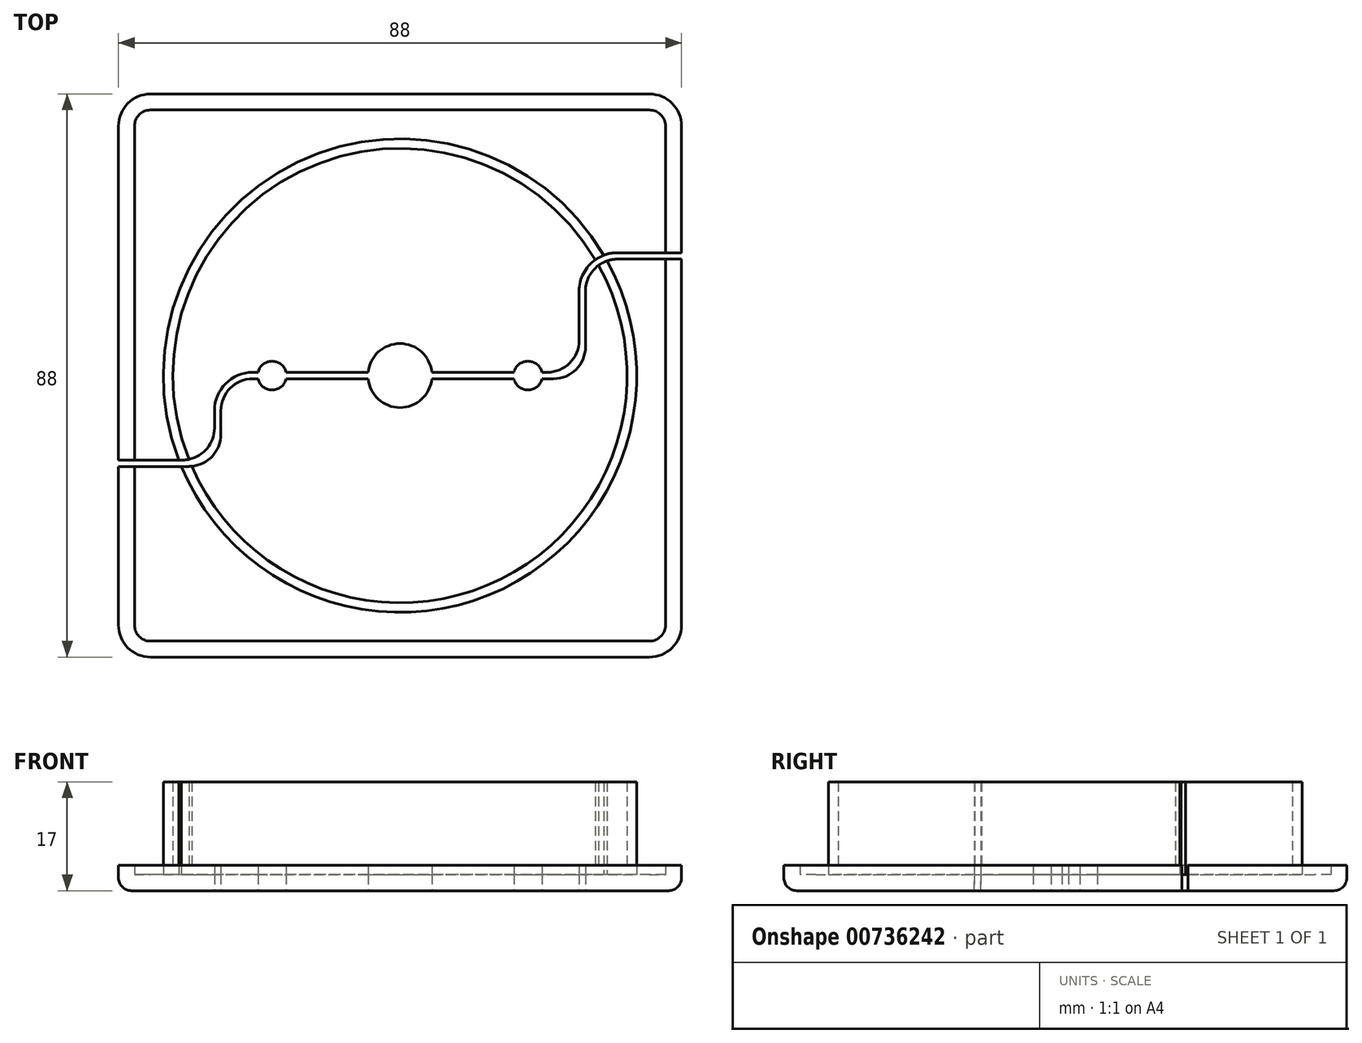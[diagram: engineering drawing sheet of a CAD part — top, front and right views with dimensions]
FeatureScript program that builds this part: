
annotation { "Feature Type Name" : "Feature", "Feature Type Description" : "" }
export const myFeature = defineFeature(function(context is Context, id is Id, definition is map)
    precondition{}
    {
        {
            var Q0;
            Q0=qCreatedBy(makeId("Top.planeOp"),FACE);
            var sketch = newSketch(context, id + "F0", { "sketchPlane" : qUnion([Q0])});
            skPoint(sketch, "E0.middle", {"position": v(0, 0) * mm});
            skLineSegment(sketch, "E1.bottom", {"start": v(39, -44) * mm, "end": v(-39, -44) * mm});
            skLineSegment(sketch, "E1.top", {"start": v(39, 44) * mm, "end": v(-39, 44) * mm});
            skLineSegment(sketch, "E1.left", {"start": v(44, -39) * mm, "end": v(44, 39) * mm});
            skLineSegment(sketch, "E1.right", {"start": v(-44, -39) * mm, "end": v(-44, 39) * mm});
            skPoint(sketch, "E2.visualSharp", {"position": v(-44, 44) * mm});
            skArc(sketch, "E2.filletArc", {"start": v(-39, 44) * mm, "mid": v(-42.54, 42.54) * mm, "end": v(-44, 39) * mm});
            skPoint(sketch, "E3.visualSharp", {"position": v(44, 44) * mm});
            skArc(sketch, "E3.filletArc", {"start": v(44, 39) * mm, "mid": v(42.54, 42.54) * mm, "end": v(39, 44) * mm});
            skPoint(sketch, "E4.visualSharp", {"position": v(44, -44) * mm});
            skArc(sketch, "E4.filletArc", {"start": v(39, -44) * mm, "mid": v(42.54, -42.54) * mm, "end": v(44, -39) * mm});
            skPoint(sketch, "E5.visualSharp", {"position": v(-44, -44) * mm});
            skArc(sketch, "E5.filletArc", {"start": v(-44, -39) * mm, "mid": v(-42.54, -42.54) * mm, "end": v(-39, -44) * mm});
            skSolve(sketch);
        }
        {
            var Q0;
            Q0=makeQuery(id+"F0.imprint","IMPRINT",FACE,{"disambiguationData":[TD([[makeQuery(id+"F0.imprint","IMPRINT",EDGE,{"derivedFrom":sQuery(id+"F0.wireOp",EDGE,"E1.bottom")}),-1.0]])]});
            extrude(context, id + "F1", {"entities" : qUnion([Q0]), "depth" : 4 * mm, "offsetDistance" : 25 * mm});
        }
        {
            var Q0;
            Q0=makeQuery(id+"F1.opExtrude","CAP_FACE",FACE,{"disambiguationData":[OSD([sQuery(id+"F0.wireOp",EDGE,"E1.bottom"),sQuery(id+"F0.wireOp",EDGE,"E1.top"),sQuery(id+"F0.wireOp",EDGE,"E1.left"),sQuery(id+"F0.wireOp",EDGE,"E1.right"),sQuery(id+"F0.wireOp",EDGE,"E2.filletArc"),sQuery(id+"F0.wireOp",EDGE,"E3.filletArc"),sQuery(id+"F0.wireOp",EDGE,"E4.filletArc"),sQuery(id+"F0.wireOp",EDGE,"E5.filletArc")])],"isStart":false});
            shell(context, id + "F2", {"entities" : qUnion([Q0]), "thickness" : 2.5 * mm});
        }
        {
            var Q0;
            Q0=makeQuery(id+"F2.opShell","OFFSET_FACE",FACE,{"disambiguationData":[OSD([sQuery(id+"F0.wireOp",EDGE,"E1.bottom"),sQuery(id+"F0.wireOp",EDGE,"E1.top"),sQuery(id+"F0.wireOp",EDGE,"E1.left"),sQuery(id+"F0.wireOp",EDGE,"E1.right"),sQuery(id+"F0.wireOp",EDGE,"E2.filletArc"),sQuery(id+"F0.wireOp",EDGE,"E3.filletArc"),sQuery(id+"F0.wireOp",EDGE,"E4.filletArc"),sQuery(id+"F0.wireOp",EDGE,"E5.filletArc")])]});
            var sketch = newSketch(context, id + "F3", { "sketchPlane" : qUnion([Q0])});
            skCircle(sketch, "E6", {"center": v(0, 0) * mm, "radius": 37 * mm});
            skSolve(sketch);
        }
        {
            var Q0;
            Q0=makeQuery(id+"F3.imprint","IMPRINT",FACE,{"disambiguationData":[TD([[makeQuery(id+"F3.imprint","IMPRINT",EDGE,{"derivedFrom":sQuery(id+"F3.wireOp",EDGE,"E6")}),1.0]])]});
            var Q1;
            Q1=sQuery(id+"F3.wireOp",EDGE,"E6");
            extrude(context, id + "F4", {"entities" : qUnion([Q0]), "surfaceEntities" : qUnion([Q1]), "depth" : 14.5 * mm, "offsetDistance" : 25 * mm});
        }
        {
            var Q0;
            Q0=makeQuery(id+"F4.opExtrude","CAP_FACE",FACE,{"disambiguationData":[OSD([sQuery(id+"F3.wireOp",EDGE,"E6")])],"isStart":false});
            shell(context, id + "F5", {"entities" : qUnion([Q0]), "thickness" : 1.5 * mm});
        }
        {
            var Q0;
            Q0=makeQuery(id+"F1.opExtrude","CAP_FACE",FACE,{"disambiguationData":[OSD([sQuery(id+"F0.wireOp",EDGE,"E1.bottom"),sQuery(id+"F0.wireOp",EDGE,"E1.top"),sQuery(id+"F0.wireOp",EDGE,"E1.left"),sQuery(id+"F0.wireOp",EDGE,"E1.right"),sQuery(id+"F0.wireOp",EDGE,"E2.filletArc"),sQuery(id+"F0.wireOp",EDGE,"E3.filletArc"),sQuery(id+"F0.wireOp",EDGE,"E4.filletArc"),sQuery(id+"F0.wireOp",EDGE,"E5.filletArc")])],"isStart":true});
            var sketch = newSketch(context, id + "F6", { "sketchPlane" : qUnion([Q0])});
            skCircle(sketch, "E7", {"center": v(0, 0) * mm, "radius": 5 * mm});
            skCircle(sketch, "E8", {"center": v(20, 0) * mm, "radius": 2.25 * mm});
            skCircle(sketch, "E9.MirrorC", {"center": v(-20, 0) * mm, "radius": 2.25 * mm});
            skSolve(sketch);
        }
        {
            var Q0;
            Q0 = qSketchRegion(id + "F6", true);
            extrude(context, id + "F7", {"entities" : qUnion([Q0]), "operationType" : NewBodyOperationType.REMOVE, "endBound" : BoundingType.THROUGH_ALL, "oppositeDirection" : true, "depth" : 25 * mm, "offsetDistance" : 25 * mm});
        }
        {
            var Q0;
            Q0=makeQuery(id+"F1.opExtrude","CAP_FACE",FACE,{"disambiguationData":[OSD([sQuery(id+"F0.wireOp",EDGE,"E1.bottom"),sQuery(id+"F0.wireOp",EDGE,"E1.top"),sQuery(id+"F0.wireOp",EDGE,"E1.left"),sQuery(id+"F0.wireOp",EDGE,"E1.right"),sQuery(id+"F0.wireOp",EDGE,"E2.filletArc"),sQuery(id+"F0.wireOp",EDGE,"E3.filletArc"),sQuery(id+"F0.wireOp",EDGE,"E4.filletArc"),sQuery(id+"F0.wireOp",EDGE,"E5.filletArc")])],"isStart":true});
            var sketch = newSketch(context, id + "F8", { "sketchPlane" : qUnion([Q0])});
            skPoint(sketch, "E10", {"position": v(0, 0) * mm});
            skLineSegment(sketch, "E11.0", {"start": v(34, -18.2) * mm, "end": v(50.26, -18.2) * mm});
            skLineSegment(sketch, "E11.1", {"start": v(-44, 14.2) * mm, "end": v(-33, 14.2) * mm});
            skLineSegment(sketch, "E11.2", {"start": v(-28, 9.2) * mm, "end": v(-28, 5.5) * mm});
            skLineSegment(sketch, "E11.3", {"start": v(-23, 0.5) * mm, "end": v(24, 0.5) * mm});
            skLineSegment(sketch, "E11.4", {"start": v(29, -4.5) * mm, "end": v(29, -13.2) * mm});
            skPoint(sketch, "E12.orphan", {"position": v(-27.24, 0) * mm});
            skPoint(sketch, "E13.start.orphan", {"position": v(27.24, 0) * mm});
            skLineSegment(sketch, "E14.0", {"start": v(34, -19.2) * mm, "end": v(50.26, -19.2) * mm});
            skLineSegment(sketch, "E14.1", {"start": v(-44, 13.2) * mm, "end": v(-34, 13.2) * mm});
            skLineSegment(sketch, "E14.2", {"start": v(-29, 8.2) * mm, "end": v(-29, 5.5) * mm});
            skLineSegment(sketch, "E14.3", {"start": v(-23, -0.5) * mm, "end": v(23, -0.5) * mm});
            skLineSegment(sketch, "E14.4", {"start": v(28, -5.5) * mm, "end": v(28, -13.2) * mm});
            skLineSegment(sketch, "E15", {"start": v(-44, 14.2) * mm, "end": v(-44, 13.2) * mm});
            skLineSegment(sketch, "E16", {"start": v(50.26, -18.2) * mm, "end": v(50.26, -19.2) * mm});
            skPoint(sketch, "E17.visualSharp", {"position": v(-29, 13.2) * mm});
            skArc(sketch, "E17.filletArc", {"start": v(-29, 8.2) * mm, "mid": v(-30.46, 11.74) * mm, "end": v(-34, 13.2) * mm});
            skPoint(sketch, "E18.visualSharp", {"position": v(-29, -0.5) * mm});
            skArc(sketch, "E18.filletArc", {"start": v(-29, 5.5) * mm, "mid": v(-27.24, 1.26) * mm, "end": v(-23, -0.5) * mm});
            skPoint(sketch, "E19.visualSharp", {"position": v(-28, 14.2) * mm});
            skArc(sketch, "E19.filletArc", {"start": v(-28, 9.2) * mm, "mid": v(-29.46, 12.74) * mm, "end": v(-33, 14.2) * mm});
            skPoint(sketch, "E20.visualSharp", {"position": v(-28, 0.5) * mm});
            skArc(sketch, "E20.filletArc", {"start": v(-28, 5.5) * mm, "mid": v(-26.54, 1.96) * mm, "end": v(-23, 0.5) * mm});
            skPoint(sketch, "E21.visualSharp", {"position": v(28, -0.5) * mm});
            skArc(sketch, "E21.filletArc", {"start": v(28, -5.5) * mm, "mid": v(26.54, -1.96) * mm, "end": v(23, -0.5) * mm});
            skPoint(sketch, "E22.visualSharp", {"position": v(28, -19.2) * mm});
            skArc(sketch, "E22.filletArc", {"start": v(28, -13.2) * mm, "mid": v(29.76, -17.44) * mm, "end": v(34, -19.2) * mm});
            skPoint(sketch, "E23.visualSharp", {"position": v(29, 0.5) * mm});
            skArc(sketch, "E23.filletArc", {"start": v(29, -4.5) * mm, "mid": v(27.54, -0.96) * mm, "end": v(24, 0.5) * mm});
            skPoint(sketch, "E24.visualSharp", {"position": v(29, -18.2) * mm});
            skArc(sketch, "E24.filletArc", {"start": v(29, -13.2) * mm, "mid": v(30.46, -16.74) * mm, "end": v(34, -18.2) * mm});
            skSolve(sketch);
        }
        {
            var Q0;
            Q0 = qSketchRegion(id + "F8", true);
            extrude(context, id + "F9", {"entities" : qUnion([Q0]), "operationType" : NewBodyOperationType.REMOVE, "endBound" : BoundingType.THROUGH_ALL, "oppositeDirection" : true, "depth" : 25 * mm, "offsetDistance" : 25 * mm});
        }
        {
            var Q0;
            Q0=makeQuery(id+"F1.opExtrude","CAP_EDGE",EDGE,{"disambiguationData":[OSD([sQuery(id+"F0.wireOp",EDGE,"E1.bottom")])],"isStart":true});
            var Q1;
            {var subQ0=sQuery(id+"F0.wireOp",EDGE,"E2.filletArc");var subQ1=sQuery(id+"F0.wireOp",EDGE,"E1.right");Q1=makeQuery(id+"F9.boolean.opBoolean","SPLIT",EDGE,{"disambiguationData":[TD([makeQuery(id+"F1.opExtrude","SWEPT_FACE",FACE,{"disambiguationData":[OSD([subQ0])]})])],"derivedFrom":makeQuery(id+"F1.opExtrude","CAP_EDGE",EDGE,{"disambiguationData":[OSD([subQ1])],"isStart":true})});}
            fillet(context, id + "F10", {"entities" : qUnion([Q0, Q1]), "radius" : 2 * mm, "tangentPropagation" : true, "allowEdgeOverflow" : false});
        }
    });
